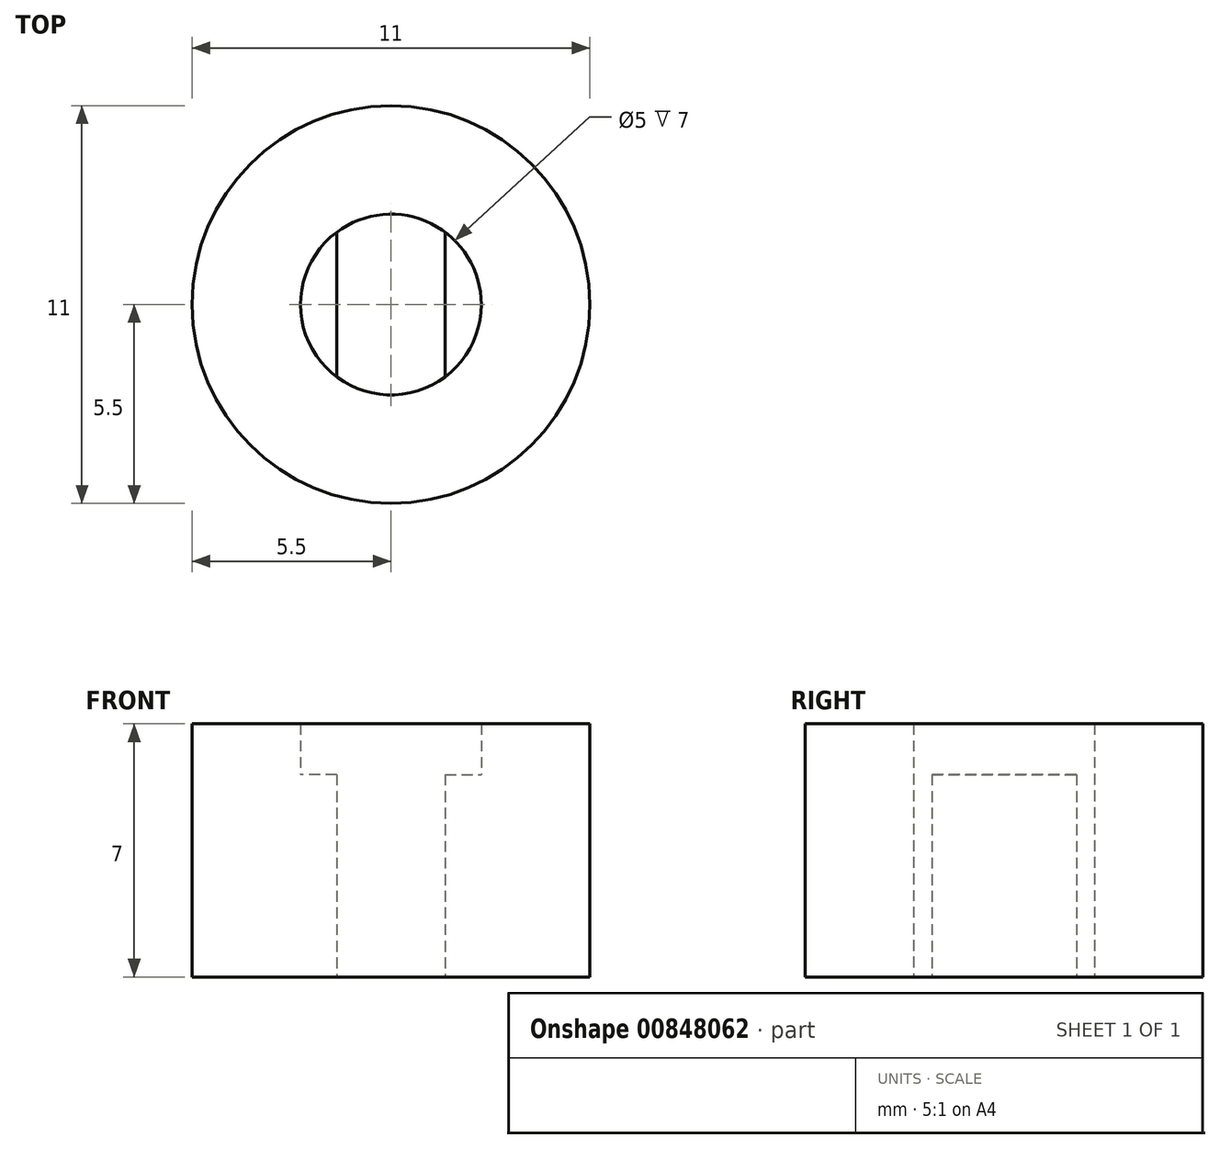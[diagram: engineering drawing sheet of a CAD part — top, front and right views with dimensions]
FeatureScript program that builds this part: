
annotation { "Feature Type Name" : "Feature", "Feature Type Description" : "" }
export const myFeature = defineFeature(function(context is Context, id is Id, definition is map)
    precondition{}
    {
        {
            var Q0;
            Q0=qCreatedBy(makeId("Top.planeOp"),FACE);
            var sketch = newSketch(context, id + "F0", { "sketchPlane" : qUnion([Q0])});
            skCircle(sketch, "E0", {"center": v(0, 0) * mm, "radius": 5.5 * mm});
            skCircle(sketch, "E1", {"center": v(0, 0) * mm, "radius": 2.5 * mm});
            skLineSegment(sketch, "E2.bottom", {"start": v(-1.5, 2) * mm, "end": v(1.5, 2) * mm});
            skLineSegment(sketch, "E2.top", {"start": v(-1.5, -2) * mm, "end": v(1.5, -2) * mm});
            skLineSegment(sketch, "E2.left", {"start": v(-1.5, 2) * mm, "end": v(-1.5, -2) * mm});
            skLineSegment(sketch, "E2.right", {"start": v(1.5, 2) * mm, "end": v(1.5, -2) * mm});
            skSolve(sketch);
        }
        {
            var Q0;
            Q0=makeQuery(id+"F0.imprint","IMPRINT",FACE,{"disambiguationData":[TD([[makeQuery(id+"F0.imprint","IMPRINT",EDGE,{"derivedFrom":sQuery(id+"F0.wireOp",EDGE,"E0")}),1.0]])]});
            var Q1;
            {var subQ0=sQuery(id+"F0.wireOp",EDGE,"E2.left");Q1=makeQuery(id+"F0.imprint","IMPRINT",FACE,{"disambiguationData":[TD([[makeQuery(id+"F0.imprint","IMPRINT",EDGE,{"derivedFrom":subQ0}),-1.0]])]});}
            var Q2;
            {var subQ0=sQuery(id+"F0.wireOp",EDGE,"E2.right");Q2=makeQuery(id+"F0.imprint","IMPRINT",FACE,{"disambiguationData":[TD([[makeQuery(id+"F0.imprint","IMPRINT",EDGE,{"derivedFrom":subQ0}),1.0]])]});}
            extrude(context, id + "F1", {"entities" : qUnion([Q0, Q1, Q2]), "depth" : 7 * mm, "offsetDistance" : 25 * mm});
        }
        {
            var Q0;
            Q0=makeQuery(id+"F1.opExtrude","CAP_FACE",FACE,{"disambiguationData":[OSD([sQuery(id+"F0.wireOp",EDGE,"E0"),sQuery(id+"F0.wireOp",EDGE,"E1"),sQuery(id+"F0.wireOp",EDGE,"E2.left"),sQuery(id+"F0.wireOp",EDGE,"E2.right")])],"isStart":false});
            var sketch = newSketch(context, id + "F2", { "sketchPlane" : qUnion([Q0])});
            skCircle(sketch, "E3.0", {"center": v(0, 0) * mm, "radius": 2.5 * mm});
            skSolve(sketch);
        }
        {
            var Q0;
            Q0 = qSketchRegion(id + "F2", true);
            extrude(context, id + "F3", {"entities" : qUnion([Q0]), "operationType" : NewBodyOperationType.REMOVE, "oppositeDirection" : true, "depth" : 1.4 * mm, "offsetDistance" : 25 * mm});
        }
    });
